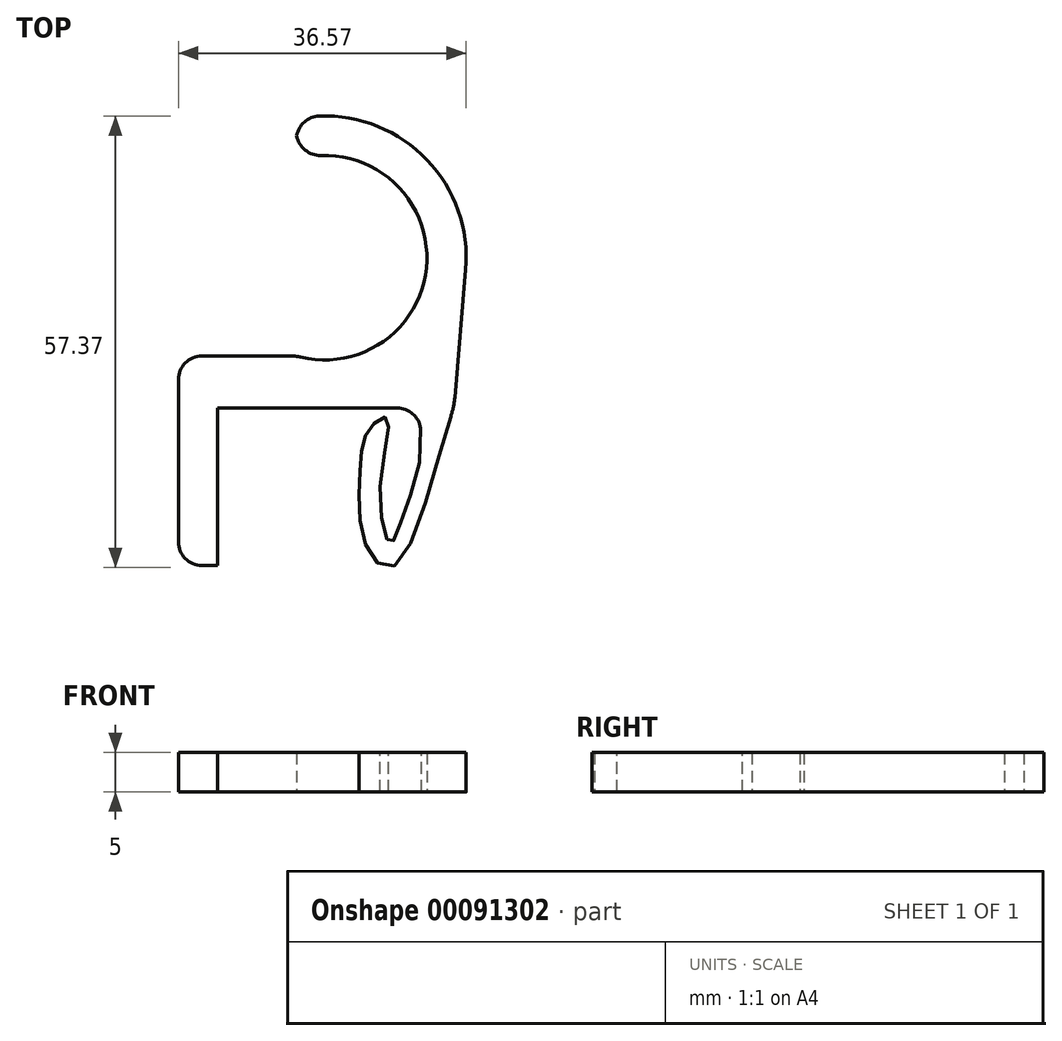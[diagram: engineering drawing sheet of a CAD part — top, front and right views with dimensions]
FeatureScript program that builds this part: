
annotation { "Feature Type Name" : "Feature", "Feature Type Description" : "" }
export const myFeature = defineFeature(function(context is Context, id is Id, definition is map)
    precondition{}
    {
        {
            assignVariable(context, id + "F0", {"name" : "Width", "anyValue" : 20});
        }
        {
            var Q0;
            Q0=qCreatedBy(makeId("Top.planeOp"),FACE);
            var sketch = newSketch(context, id + "F1", { "sketchPlane" : qUnion([Q0])});
            skLineSegment(sketch, "E0", {"start": v(-10, 0) * mm, "end": v(10, 0) * mm});
            skLineSegment(sketch, "E1", {"start": v(-10, 0) * mm, "end": v(-10, -20) * mm});
            skLineSegment(sketch, "E2", {"start": v(-10, -20) * mm, "end": v(-15, -20) * mm});
            skLineSegment(sketch, "E3", {"start": v(-15, -20) * mm, "end": v(-15, 6.6) * mm});
            skLineSegment(sketch, "E4", {"start": v(-15, 6.6) * mm, "end": v(0, 6.6) * mm});
            skLineSegment(sketch, "E5", {"start": v(0, 6.6) * mm, "end": v(0, 31.6) * mm, "construction": true});
            skArc(sketch, "E6", {"start": v(0, 6.6) * mm, "mid": v(16.57, 19.1) * mm, "end": v(0, 31.6) * mm});
            skLineSegment(sketch, "E7", {"start": v(10, 0) * mm, "end": v(20, 0) * mm});
            skPoint(sketch, "E8.endSnap0", {"position": v(15, 0) * mm});
            skFitSpline(sketch, "E9", {"points": [v(20, 0) * mm, v(12.53, -20) * mm, v(8.95, -17.8) * mm, v(8, -9.54) * mm, v(8.53, -4.24) * mm, v(10, -1.83) * mm, v(11.52, -1.26) * mm, v(10.64, -10) * mm, v(11.93, -17.12) * mm, v(13.44, -14) * mm, v(15, 0) * mm], "startDerivative": vector(-32.03, -80.59) * mm, "endDerivative": vector(-45.23, 94.9) * mm});
            skLineSegment(sketch, "E10", {"start": v(10, 0) * mm, "end": v(10, -20) * mm, "construction": true});
            skArc(sketch, "E11.0", {"start": v(0.35, 1.4) * mm, "mid": v(21.57, 19.28) * mm, "end": v(0, 36.74) * mm});
            skLineSegment(sketch, "E12", {"start": v(0, 31.6) * mm, "end": v(0, 36.74) * mm});
            skLineSegment(sketch, "E13", {"start": v(21.5, 17.56) * mm, "end": v(20, 0) * mm});
            skLineSegment(sketch, "E14", {"start": v(0.35, 1.4) * mm, "end": v(0, 0) * mm});
            skPoint(sketch, "E15", {"position": v(10, -10) * mm});
            skSolve(sketch);
        }
        {
            var Q0;
            Q0 = qSketchRegion(id + "F1", true);
            extrude(context, id + "F2", {"entities" : qUnion([Q0]), "depth" : (getVariable(context, 'Width') / 4) * mm, "offsetDistance" : 25 * mm});
        }
        {
            var Q0;
            Q0=makeQuery(id+"F2.opExtrude","SWEPT_EDGE",EDGE,{"disambiguationData":[OSD([sQuery(id+"F1.wireOp",EDGE,"E4"),sQuery(id+"F1.wireOp",EDGE,"E6")])]});
            fillet(context, id + "F3", {"entities" : qUnion([Q0]), "radius" : 5 * mm, "tangentPropagation" : true, "allowEdgeOverflow" : false});
        }
        {
            var Q0;
            Q0=makeQuery(id+"F2.opExtrude","SWEPT_EDGE",EDGE,{"disambiguationData":[OSD([sQuery(id+"F1.wireOp",EDGE,"E6"),sQuery(id+"F1.wireOp",EDGE,"E12")])]});
            var Q1;
            Q1=makeQuery(id+"F2.opExtrude","SWEPT_EDGE",EDGE,{"disambiguationData":[OSD([sQuery(id+"F1.wireOp",EDGE,"E11.0"),sQuery(id+"F1.wireOp",EDGE,"E12")])]});
            var Q2;
            Q2=makeQuery(id+"F2.opExtrude","SWEPT_EDGE",EDGE,{"disambiguationData":[OSD([sQuery(id+"F1.wireOp",EDGE,"E3"),sQuery(id+"F1.wireOp",EDGE,"E4")])]});
            var Q3;
            Q3=makeQuery(id+"F2.opExtrude","SWEPT_EDGE",EDGE,{"disambiguationData":[OSD([sQuery(id+"F1.wireOp",EDGE,"E2"),sQuery(id+"F1.wireOp",EDGE,"E3")])]});
            var Q4;
            Q4=makeQuery(id+"F2.opExtrude","SWEPT_EDGE",EDGE,{"disambiguationData":[OSD([sQuery(id+"F1.wireOp",EDGE,"E7"),sQuery(id+"F1.wireOp",EDGE,"E9")])]});
            fillet(context, id + "F4", {"entities" : qUnion([Q0, Q1, Q2, Q3, Q4]), "radius" : 3 * mm, "tangentPropagation" : true, "allowEdgeOverflow" : false});
        }
        {
            var Q0;
            Q0=makeQuery(id+"F2.opExtrude","SWEPT_EDGE",EDGE,{"disambiguationData":[OSD([sQuery(id+"F1.wireOp",EDGE,"E7"),sQuery(id+"F1.wireOp",EDGE,"E9"),sQuery(id+"F1.wireOp",EDGE,"E13")])]});
            fillet(context, id + "F5", {"entities" : qUnion([Q0]), "radius" : 10 * mm, "tangentPropagation" : true, "allowEdgeOverflow" : false});
        }
    });
